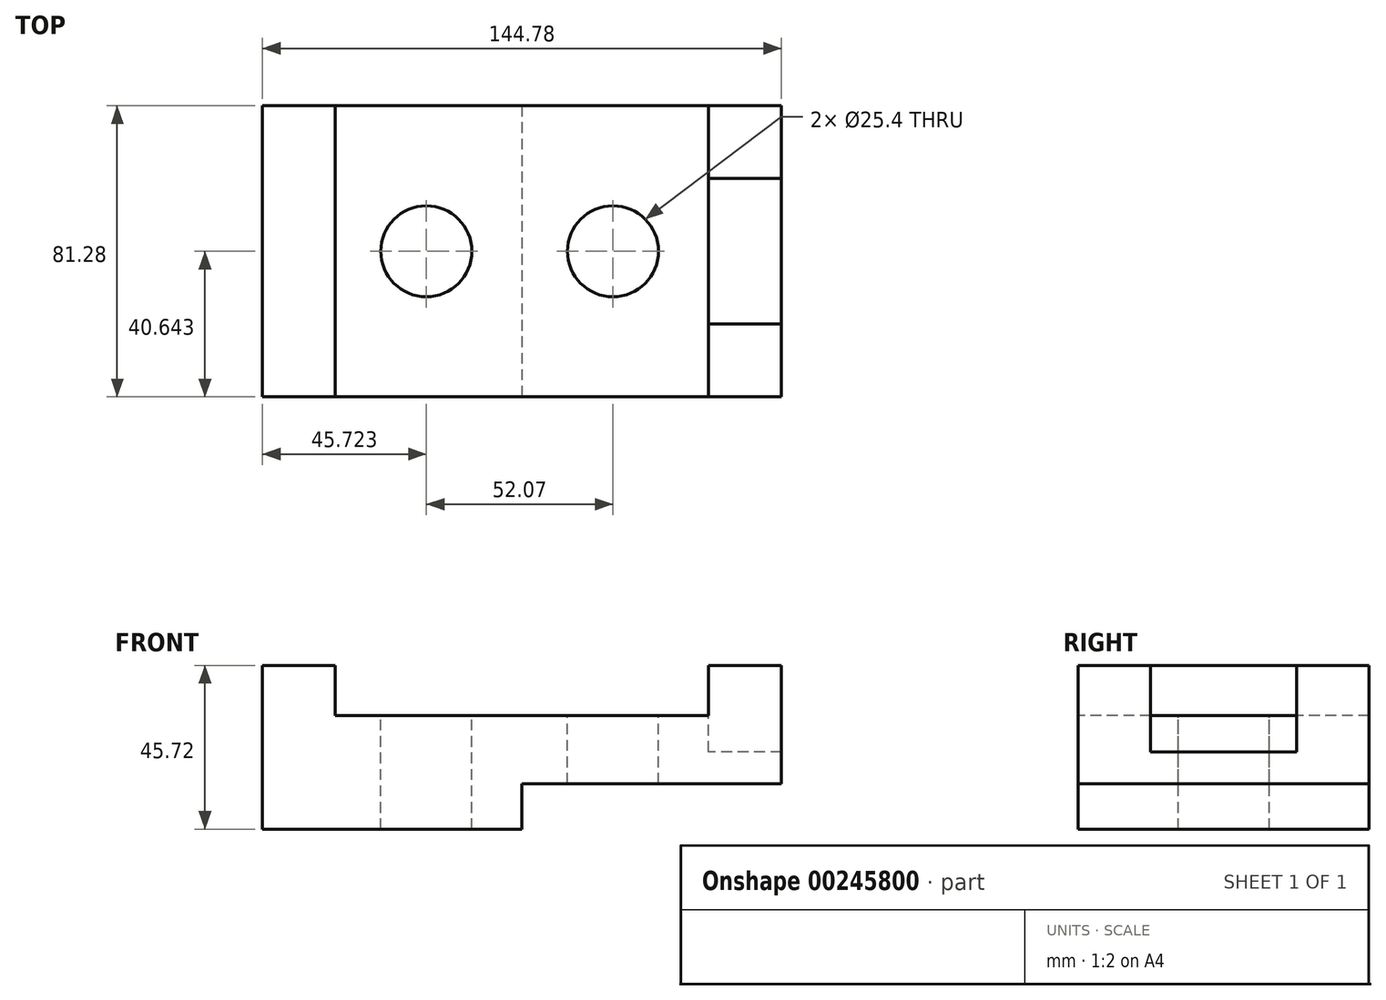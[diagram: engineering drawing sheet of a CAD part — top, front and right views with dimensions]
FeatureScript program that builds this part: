
annotation { "Feature Type Name" : "Feature", "Feature Type Description" : "" }
export const myFeature = defineFeature(function(context is Context, id is Id, definition is map)
    precondition{}
    {
        {
            var Q0;
            Q0=qCreatedBy(makeId("Top.planeOp"),FACE);
            var sketch = newSketch(context, id + "F0", { "sketchPlane" : qUnion([Q0])});
            skLineSegment(sketch, "E0.bottom", {"start": v(-70.82, 50.11) * mm, "end": v(73.96, 50.11) * mm});
            skLineSegment(sketch, "E0.top", {"start": v(-70.82, -31.17) * mm, "end": v(73.96, -31.17) * mm});
            skLineSegment(sketch, "E0.left", {"start": v(-70.82, 50.11) * mm, "end": v(-70.82, -31.17) * mm});
            skLineSegment(sketch, "E0.right", {"start": v(73.96, 50.11) * mm, "end": v(73.96, -31.17) * mm});
            skSolve(sketch);
        }
        {
            var Q0;
            Q0 = qSketchRegion(id + "F0", true);
            extrude(context, id + "F1", {"entities" : qUnion([Q0]), "depth" : 45.72 * mm});
        }
        {
            var Q0;
            Q0=makeQuery(id+"F1.opExtrude","CAP_FACE",FACE,{"disambiguationData":[OSD([sQuery(id+"F0.wireOp",EDGE,"E0.bottom"),sQuery(id+"F0.wireOp",EDGE,"E0.top"),sQuery(id+"F0.wireOp",EDGE,"E0.left"),sQuery(id+"F0.wireOp",EDGE,"E0.right")])],"isStart":false});
            var sketch = newSketch(context, id + "F2", { "sketchPlane" : qUnion([Q0])});
            skLineSegment(sketch, "E1.bottom", {"start": v(-50.5, 50.11) * mm, "end": v(53.64, 50.11) * mm});
            skLineSegment(sketch, "E1.top", {"start": v(-50.5, -31.17) * mm, "end": v(53.64, -31.17) * mm});
            skLineSegment(sketch, "E1.left", {"start": v(-50.5, 50.11) * mm, "end": v(-50.5, -31.17) * mm});
            skLineSegment(sketch, "E1.right", {"start": v(53.64, 50.11) * mm, "end": v(53.64, -31.17) * mm});
            skSolve(sketch);
        }
        {
            var Q0;
            Q0=makeQuery(id+"F2.imprint","IMPRINT",FACE,{"disambiguationData":[TD([[makeQuery(id+"F2.imprint","IMPRINT",EDGE,{"derivedFrom":sQuery(id+"F2.wireOp",EDGE,"E1.bottom")}),-1.0]])]});
            extrude(context, id + "F3", {"entities" : qUnion([Q0]), "operationType" : NewBodyOperationType.REMOVE, "oppositeDirection" : true, "depth" : 13.97 * mm});
        }
        {
            var Q0;
            {var subQ0=sQuery(id+"F0.wireOp",EDGE,"E0.bottom");var subQ1=sQuery(id+"F0.wireOp",EDGE,"E0.top");var subQ2=sQuery(id+"F0.wireOp",EDGE,"E0.right");Q0=makeQuery(id+"F3.boolean.opBoolean","SPLIT",FACE,{"disambiguationData":[TD([makeQuery(id+"F1.opExtrude","SWEPT_FACE",FACE,{"disambiguationData":[OSD([subQ2])]})])],"derivedFrom":makeQuery(id+"F1.opExtrude","CAP_FACE",FACE,{"disambiguationData":[OSD([subQ0,subQ1,sQuery(id+"F0.wireOp",EDGE,"E0.left"),subQ2])],"isStart":false})});}
            var sketch = newSketch(context, id + "F4", { "sketchPlane" : qUnion([Q0])});
            skLineSegment(sketch, "E2.bottom", {"start": v(73.96, 29.8) * mm, "end": v(53.64, 29.8) * mm});
            skLineSegment(sketch, "E2.top", {"start": v(73.96, -10.85) * mm, "end": v(53.64, -10.85) * mm});
            skLineSegment(sketch, "E2.left", {"start": v(73.96, 29.8) * mm, "end": v(73.96, -10.85) * mm});
            skLineSegment(sketch, "E2.right", {"start": v(53.64, 29.8) * mm, "end": v(53.64, -10.85) * mm});
            skSolve(sketch);
        }
        {
            var Q0;
            Q0=makeQuery(id+"F4.imprint","IMPRINT",FACE,{"disambiguationData":[TD([[makeQuery(id+"F4.imprint","IMPRINT",EDGE,{"derivedFrom":sQuery(id+"F4.wireOp",EDGE,"E2.bottom")}),1.0]])]});
            extrude(context, id + "F5", {"entities" : qUnion([Q0]), "operationType" : NewBodyOperationType.REMOVE, "oppositeDirection" : true, "depth" : 24.13 * mm});
        }
        {
            var Q0;
            Q0=makeQuery(id+"F1.opExtrude","CAP_FACE",FACE,{"disambiguationData":[OSD([sQuery(id+"F0.wireOp",EDGE,"E0.bottom"),sQuery(id+"F0.wireOp",EDGE,"E0.top"),sQuery(id+"F0.wireOp",EDGE,"E0.left"),sQuery(id+"F0.wireOp",EDGE,"E0.right")])],"isStart":true});
            var sketch = newSketch(context, id + "F6", { "sketchPlane" : qUnion([Q0])});
            skLineSegment(sketch, "E3.bottom", {"start": v(73.96, -50.11) * mm, "end": v(1.57, -50.11) * mm});
            skLineSegment(sketch, "E3.top", {"start": v(73.96, 31.17) * mm, "end": v(1.57, 31.17) * mm});
            skLineSegment(sketch, "E3.left", {"start": v(73.96, -50.11) * mm, "end": v(73.96, 31.17) * mm});
            skLineSegment(sketch, "E3.right", {"start": v(1.57, -50.11) * mm, "end": v(1.57, 31.17) * mm});
            skSolve(sketch);
        }
        {
            var Q0;
            Q0=makeQuery(id+"F6.imprint","IMPRINT",FACE,{"disambiguationData":[TD([[makeQuery(id+"F6.imprint","IMPRINT",EDGE,{"derivedFrom":sQuery(id+"F6.wireOp",EDGE,"E3.bottom")}),1.0]])]});
            extrude(context, id + "F7", {"entities" : qUnion([Q0]), "operationType" : NewBodyOperationType.REMOVE, "oppositeDirection" : true, "depth" : 12.7 * mm});
        }
        {
            var Q0;
            Q0=makeQuery(id+"F3.boolean.opBoolean","COPY",FACE,{"derivedFrom":makeQuery(id+"F3.opExtrude","CAP_FACE",FACE,{"disambiguationData":[OSD([sQuery(id+"F2.wireOp",EDGE,"E1.bottom"),sQuery(id+"F2.wireOp",EDGE,"E1.top"),sQuery(id+"F2.wireOp",EDGE,"E1.left"),sQuery(id+"F2.wireOp",EDGE,"E1.right")])],"isStart":false})});
            var sketch = newSketch(context, id + "F8", { "sketchPlane" : qUnion([Q0])});
            skCircle(sketch, "E4", {"center": v(-25.1, 9.47) * mm, "radius": 12.7 * mm});
            skCircle(sketch, "E5", {"center": v(26.97, 9.47) * mm, "radius": 12.7 * mm});
            skSolve(sketch);
        }
        {
            var Q0;
            Q0=makeQuery(id+"F8.imprint","IMPRINT",FACE,{"disambiguationData":[TD([[makeQuery(id+"F8.imprint","IMPRINT",EDGE,{"derivedFrom":sQuery(id+"F8.wireOp",EDGE,"E4")}),1.0]])]});
            var Q1;
            Q1=sQuery(id+"F8.wireOp",EDGE,"E4");
            extrude(context, id + "F9", {"entities" : qUnion([Q0]), "operationType" : NewBodyOperationType.REMOVE, "surfaceEntities" : qUnion([Q1]), "oppositeDirection" : true, "depth" : 32 * mm});
        }
        {
            var Q0;
            Q0=makeQuery(id+"F3.boolean.opBoolean","COPY",FACE,{"derivedFrom":makeQuery(id+"F3.opExtrude","CAP_FACE",FACE,{"disambiguationData":[OSD([sQuery(id+"F2.wireOp",EDGE,"E1.bottom"),sQuery(id+"F2.wireOp",EDGE,"E1.top"),sQuery(id+"F2.wireOp",EDGE,"E1.left"),sQuery(id+"F2.wireOp",EDGE,"E1.right")])],"isStart":false})});
            var sketch = newSketch(context, id + "F10", { "sketchPlane" : qUnion([Q0])});
            skCircle(sketch, "E6", {"center": v(26.97, 9.47) * mm, "radius": 12.7 * mm});
            skSolve(sketch);
        }
        {
            var Q0;
            Q0=makeQuery(id+"F10.imprint","IMPRINT",FACE,{"disambiguationData":[TD([[makeQuery(id+"F10.imprint","IMPRINT",EDGE,{"derivedFrom":sQuery(id+"F10.wireOp",EDGE,"E6")}),1.0]])]});
            extrude(context, id + "F11", {"entities" : qUnion([Q0]), "operationType" : NewBodyOperationType.REMOVE, "oppositeDirection" : true, "depth" : 19.56 * mm});
        }
    });
